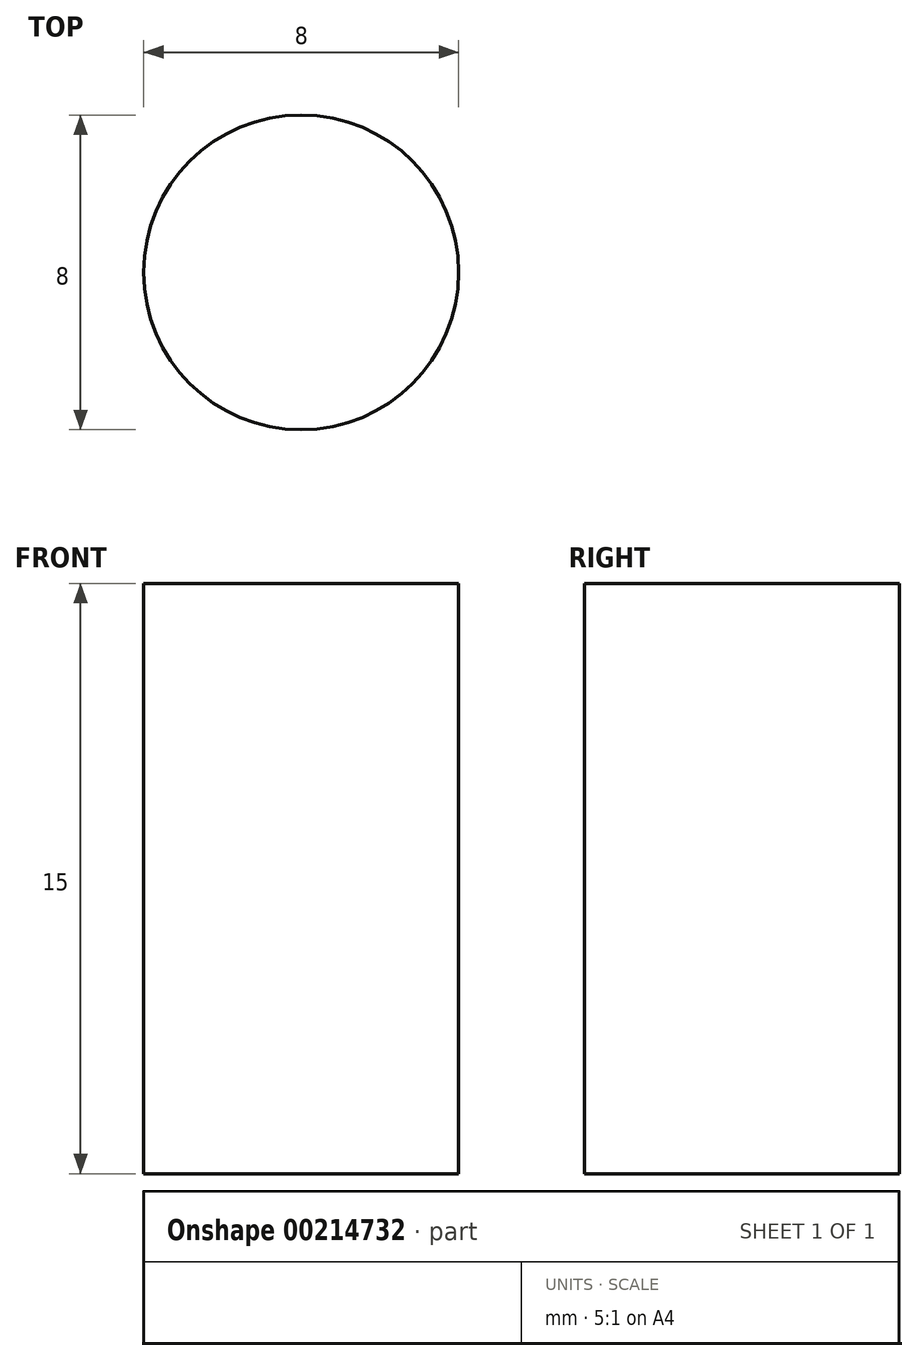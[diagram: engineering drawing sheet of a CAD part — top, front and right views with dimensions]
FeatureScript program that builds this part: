
annotation { "Feature Type Name" : "Feature", "Feature Type Description" : "" }
export const myFeature = defineFeature(function(context is Context, id is Id, definition is map)
    precondition{}
    {
        {
            var Q0;
            Q0=qCreatedBy(makeId("Top.planeOp"),FACE);
            var sketch = newSketch(context, id + "F0", { "sketchPlane" : qUnion([Q0])});
            skCircle(sketch, "E0", {"center": v(0, 0) * mm, "radius": 4 * mm});
            skSolve(sketch);
        }
        {
            var Q0;
            Q0=makeQuery(id+"F0.imprint","IMPRINT",FACE,{"disambiguationData":[TD([[makeQuery(id+"F0.imprint","IMPRINT",EDGE,{"derivedFrom":sQuery(id+"F0.wireOp",EDGE,"E0")}),1.0]])]});
            extrude(context, id + "F1", {"entities" : qUnion([Q0]), "depth" : 15 * mm});
        }
    });
